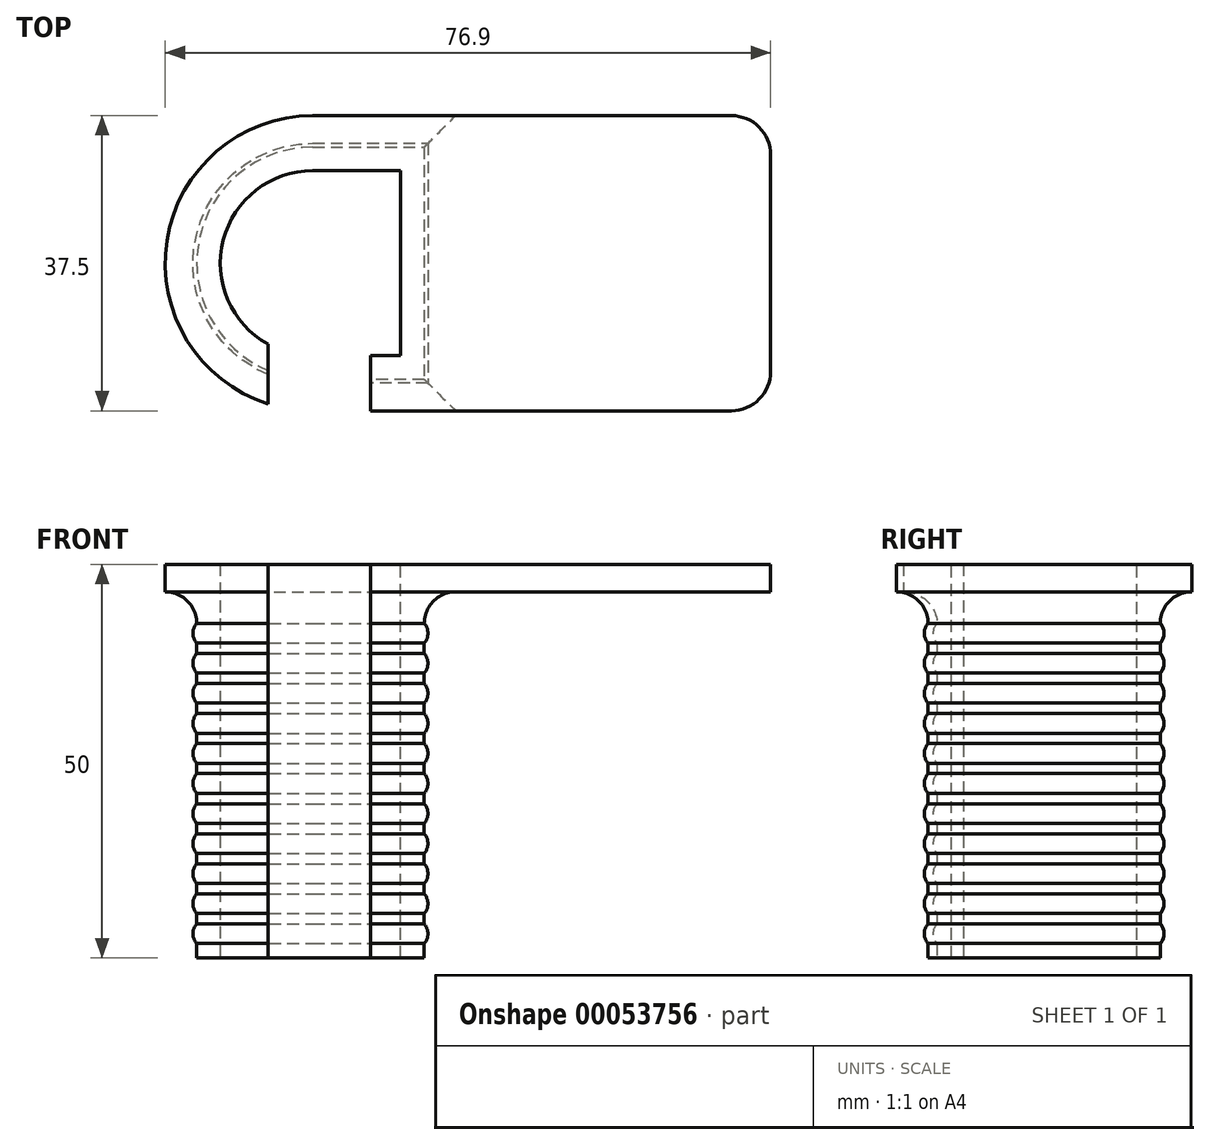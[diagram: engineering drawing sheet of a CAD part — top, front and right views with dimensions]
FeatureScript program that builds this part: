
annotation { "Feature Type Name" : "Feature", "Feature Type Description" : "" }
export const myFeature = defineFeature(function(context is Context, id is Id, definition is map)
    precondition{}
    {
        {
            var Q0;
            Q0=qCreatedBy(makeId("Top.planeOp"),FACE);
            var sketch = newSketch(context, id + "F0", { "sketchPlane" : qUnion([Q0])});
            skLineSegment(sketch, "E0", {"start": v(0, 0) * mm, "end": v(0, 23.5) * mm});
            skLineSegment(sketch, "E1", {"start": v(0, 23.5) * mm, "end": v(-11.15, 23.5) * mm});
            skLineSegment(sketch, "E2", {"start": v(0, 0) * mm, "end": v(-11.15, 0) * mm});
            skArc(sketch, "E3", {"start": v(-11.15, 23.5) * mm, "mid": v(-22.9, 11.75) * mm, "end": v(-11.15, 0) * mm});
            skSolve(sketch);
        }
        {
            var Q0;
            Q0=qCreatedBy(makeId("Right.planeOp"),FACE);
            var sketch = newSketch(context, id + "F1", { "sketchPlane" : qUnion([Q0])});
            skLineSegment(sketch, "E4", {"start": v(-3.5, 0) * mm, "end": v(-3.5, 50) * mm, "construction": true});
            skLineSegment(sketch, "E5", {"start": v(0, 0) * mm, "end": v(0, 50) * mm});
            skLineSegment(sketch, "E6", {"start": v(0, 0) * mm, "end": v(-3.5, 0) * mm});
            skLineSegment(sketch, "E7", {"start": v(-3.5, 50) * mm, "end": v(0, 50) * mm});
            skLineSegment(sketch, "E8", {"start": v(-3, 46.5) * mm, "end": v(-3, 46.3) * mm});
            skArc(sketch, "E9", {"start": v(-3, 4.32) * mm, "mid": v(-3.48, 3.07) * mm, "end": v(-3, 1.82) * mm});
            skLineSegment(sketch, "E10", {"start": v(-1.6, 0) * mm, "end": v(-1.6, 50) * mm, "construction": true});
            skArc(sketch, "E11.1.0.0", {"start": v(-3, 8.13) * mm, "mid": v(-3.48, 6.88) * mm, "end": v(-3, 5.63) * mm});
            skArc(sketch, "E11.2.0.0", {"start": v(-3, 11.95) * mm, "mid": v(-3.48, 10.7) * mm, "end": v(-3, 9.45) * mm});
            skArc(sketch, "E11.3.0.0", {"start": v(-3, 15.77) * mm, "mid": v(-3.48, 14.52) * mm, "end": v(-3, 13.27) * mm});
            skLineSegment(sketch, "E11.direction1", {"start": v(-3, 1.82) * mm, "end": v(-3, 5.63) * mm, "construction": true});
            skLineSegment(sketch, "E12.trimOffspring", {"start": v(-3, 13.27) * mm, "end": v(-3, 11.95) * mm});
            skLineSegment(sketch, "E13.trimOffspring", {"start": v(-3, 9.45) * mm, "end": v(-3, 8.13) * mm});
            skLineSegment(sketch, "E14.trimOffspring", {"start": v(-3, 5.63) * mm, "end": v(-3, 4.32) * mm});
            skLineSegment(sketch, "E15.trimOffspring", {"start": v(-3, 1.82) * mm, "end": v(-3, 0) * mm});
            skArc(sketch, "E16.0.4.0", {"start": v(-3, 19.59) * mm, "mid": v(-3.48, 18.34) * mm, "end": v(-3, 17.09) * mm});
            skArc(sketch, "E16.0.5.0", {"start": v(-3, 23.4) * mm, "mid": v(-3.48, 22.15) * mm, "end": v(-3, 20.9) * mm});
            skArc(sketch, "E16.0.6.0", {"start": v(-3, 27.22) * mm, "mid": v(-3.48, 25.97) * mm, "end": v(-3, 24.72) * mm});
            skArc(sketch, "E16.0.7.0", {"start": v(-3, 31.04) * mm, "mid": v(-3.48, 29.79) * mm, "end": v(-3, 28.54) * mm});
            skArc(sketch, "E17.0.8.0", {"start": v(-3, 34.86) * mm, "mid": v(-3.48, 33.6) * mm, "end": v(-3, 32.36) * mm});
            skArc(sketch, "E17.0.9.0", {"start": v(-3, 38.67) * mm, "mid": v(-3.48, 37.42) * mm, "end": v(-3, 36.17) * mm});
            skArc(sketch, "E17.0.10.0", {"start": v(-3, 42.5) * mm, "mid": v(-3.48, 41.24) * mm, "end": v(-3, 40) * mm});
            skLineSegment(sketch, "E18.trimOffspring", {"start": v(-3, 43.8) * mm, "end": v(-3, 42.5) * mm});
            skLineSegment(sketch, "E19.trimOffspring", {"start": v(-3, 40) * mm, "end": v(-3, 38.67) * mm});
            skLineSegment(sketch, "E20.trimOffspring", {"start": v(-3, 36.17) * mm, "end": v(-3, 34.86) * mm});
            skLineSegment(sketch, "E21.trimOffspring", {"start": v(-3, 32.36) * mm, "end": v(-3, 31.04) * mm});
            skLineSegment(sketch, "E22.trimOffspring", {"start": v(-3, 28.54) * mm, "end": v(-3, 27.22) * mm});
            skLineSegment(sketch, "E23.trimOffspring", {"start": v(-3, 24.72) * mm, "end": v(-3, 23.4) * mm});
            skLineSegment(sketch, "E24.trimOffspring", {"start": v(-3, 20.9) * mm, "end": v(-3, 19.59) * mm});
            skLineSegment(sketch, "E25.trimOffspring", {"start": v(-3, 17.09) * mm, "end": v(-3, 15.77) * mm});
            skPoint(sketch, "E26.0.end.orphan", {"position": v(17.28, -22.16) * mm});
            skPoint(sketch, "E26.0.start.orphan", {"position": v(0, 0) * mm});
            skLineSegment(sketch, "E27", {"start": v(-3, 46.3) * mm, "end": v(-3, 43.8) * mm});
            skLineSegment(sketch, "E28.bottom", {"start": v(-3, 50) * mm, "end": v(-7, 50) * mm});
            skLineSegment(sketch, "E28.top", {"start": v(-3, 46.5) * mm, "end": v(-7, 46.5) * mm});
            skLineSegment(sketch, "E28.right", {"start": v(-7, 50) * mm, "end": v(-7, 46.5) * mm});
            skSolve(sketch);
        }
        {
            var Q0;
            {var subQ2=sQuery(id+"F1.wireOp",EDGE,"E5");Q0=makeQuery(id+"F1.imprint","IMPRINT",FACE,{"disambiguationData":[TD([[makeQuery(id+"F1.imprint","IMPRINT",EDGE,{"derivedFrom":subQ2}),1.0]])]});}
            var Q1;
            Q1=sQuery(id+"F0.wireOp",EDGE,"E2");
            var Q2;
            Q2=sQuery(id+"F0.wireOp",EDGE,"E3");
            var Q3;
            Q3=sQuery(id+"F0.wireOp",EDGE,"E1");
            var Q4;
            Q4=sQuery(id+"F0.wireOp",EDGE,"E0");
            sweep(context, id + "F2", {"profiles" : qUnion([Q0]), "path" : qUnion([Q1, Q2, Q3, Q4])});
        }
        {
            var Q0;
            Q0=qCreatedBy(makeId("Front.planeOp"),FACE);
            cPlane(context, id + "F3", {"entities" : qUnion([Q0]), "cplaneType" : CPlaneType.OFFSET, "offset" : 10 * mm, "width" : 150 * mm, "height" : 150 * mm});
        }
        {
            var Q0;
            Q0=qCreatedBy(id+"F3.planeOp",FACE);
            var sketch = newSketch(context, id + "F4", { "sketchPlane" : qUnion([Q0])});
            skLineSegment(sketch, "E29.0", {"start": v(-11.15, 46.5) * mm, "end": v(-11.15, 42.5) * mm, "construction": true});
            skLineSegment(sketch, "E30.bottom", {"start": v(-16.85, 57.69) * mm, "end": v(-3.85, 57.69) * mm});
            skLineSegment(sketch, "E30.top", {"start": v(-16.85, -9.13) * mm, "end": v(-3.85, -9.13) * mm});
            skLineSegment(sketch, "E30.left", {"start": v(-16.85, 57.69) * mm, "end": v(-16.85, -9.13) * mm});
            skLineSegment(sketch, "E30.right", {"start": v(-3.85, 57.69) * mm, "end": v(-3.85, -9.13) * mm});
            skSolve(sketch);
        }
        {
            var Q0;
            Q0=makeQuery(id+"F4.imprint","IMPRINT",FACE,{"disambiguationData":[TD([[makeQuery(id+"F4.imprint","IMPRINT",EDGE,{"derivedFrom":sQuery(id+"F4.wireOp",EDGE,"E30.bottom")}),-1.0]])]});
            extrude(context, id + "F5", {"entities" : qUnion([Q0]), "operationType" : NewBodyOperationType.REMOVE, "oppositeDirection" : true, "depth" : 13.38 * mm});
        }
        {
            var Q0;
            Q0=makeQuery(id+"F2.opSweep","SWEPT_FACE",FACE,{"disambiguationData":[OSD([sQuery(id+"F0.wireOp",EDGE,"E0"),sQuery(id+"F1.wireOp",EDGE,"E28.right")])]});
            extrude(context, id + "F6", {"entities" : qUnion([Q0]), "operationType" : NewBodyOperationType.ADD, "depth" : 40 * mm});
        }
        {
            var Q0;
            Q0=makeQuery(id+"F6.opExtrude","CAP_EDGE",EDGE,{"disambiguationData":[OSD([sQuery(id+"F0.wireOp",VERTEX,"E0.end"),sQuery(id+"F1.wireOp",EDGE,"E28.right")])],"isStart":false});
            var Q1;
            Q1=makeQuery(id+"F6.opExtrude","CAP_EDGE",EDGE,{"disambiguationData":[OSD([sQuery(id+"F0.wireOp",VERTEX,"E0.start"),sQuery(id+"F1.wireOp",EDGE,"E28.right")])],"isStart":false});
            fillet(context, id + "F7", {"entities" : qUnion([Q0, Q1]), "radius" : 5 * mm, "tangentPropagation" : true, "allowEdgeOverflow" : false});
        }
        {
            var Q0;
            Q0=makeQuery(id+"F2.opSweep","SWEPT_EDGE",EDGE,{"disambiguationData":[OSD([sQuery(id+"F0.wireOp",EDGE,"E0"),sQuery(id+"F1.wireOp",EDGE,"E8"),sQuery(id+"F1.wireOp",EDGE,"E28.top")])]});
            var Q1;
            Q1=makeQuery(id+"F2.opSweep","SWEPT_EDGE",EDGE,{"disambiguationData":[OSD([sQuery(id+"F0.wireOp",EDGE,"E1"),sQuery(id+"F1.wireOp",EDGE,"E8"),sQuery(id+"F1.wireOp",EDGE,"E28.top")])]});
            var Q2;
            Q2=makeQuery(id+"F2.opSweep","SWEPT_EDGE",EDGE,{"disambiguationData":[OSD([sQuery(id+"F0.wireOp",EDGE,"E3"),sQuery(id+"F1.wireOp",EDGE,"E8"),sQuery(id+"F1.wireOp",EDGE,"E28.top")])]});
            var Q3;
            Q3=makeQuery(id+"F2.opSweep","SWEPT_EDGE",EDGE,{"disambiguationData":[OSD([sQuery(id+"F0.wireOp",EDGE,"E2"),sQuery(id+"F1.wireOp",EDGE,"E8"),sQuery(id+"F1.wireOp",EDGE,"E28.top")])]});
            fillet(context, id + "F8", {"entities" : qUnion([Q0, Q1, Q2, Q3]), "radius" : 4 * mm, "tangentPropagation" : true, "allowEdgeOverflow" : false});
        }
    });
